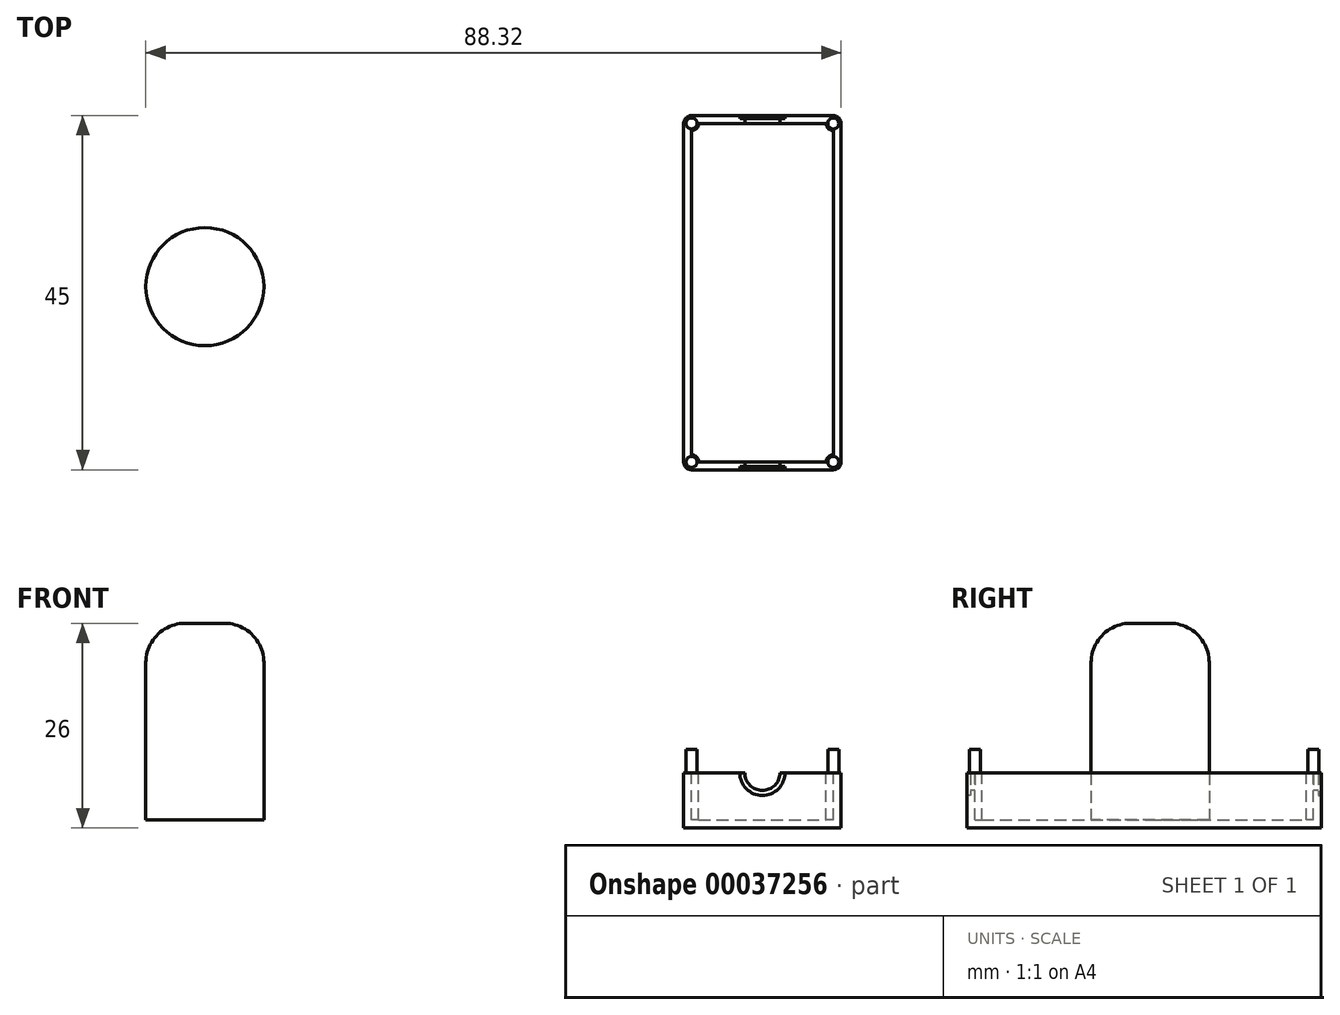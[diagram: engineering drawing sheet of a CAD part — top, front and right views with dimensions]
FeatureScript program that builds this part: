
annotation { "Feature Type Name" : "Feature", "Feature Type Description" : "" }
export const myFeature = defineFeature(function(context is Context, id is Id, definition is map)
    precondition{}
    {
        {
            var Q0;
            Q0=qCreatedBy(makeId("Top.planeOp"),FACE);
            var sketch = newSketch(context, id + "F0", { "sketchPlane" : qUnion([Q0])});
            skLineSegment(sketch, "E0.bottom", {"start": v(0, 0) * mm, "end": v(20, 0) * mm});
            skLineSegment(sketch, "E0.top", {"start": v(0, 45) * mm, "end": v(20, 45) * mm});
            skLineSegment(sketch, "E0.left", {"start": v(0, 0) * mm, "end": v(0, 45) * mm});
            skLineSegment(sketch, "E0.right", {"start": v(20, 0) * mm, "end": v(20, 45) * mm});
            skLineSegment(sketch, "E1.0", {"start": v(19, 1) * mm, "end": v(19, 44) * mm});
            skLineSegment(sketch, "E1.1", {"start": v(1, 1) * mm, "end": v(19, 1) * mm});
            skLineSegment(sketch, "E1.2", {"start": v(1, 1) * mm, "end": v(1, 44) * mm});
            skLineSegment(sketch, "E1.3", {"start": v(1, 44) * mm, "end": v(19, 44) * mm});
            skSolve(sketch);
        }
        {
            var Q0;
            Q0=makeQuery(id+"F0.imprint","IMPRINT",FACE,{"disambiguationData":[TD([[makeQuery(id+"F0.imprint","IMPRINT",EDGE,{"derivedFrom":sQuery(id+"F0.wireOp",EDGE,"E0.bottom")}),1.0]])]});
            extrude(context, id + "F1", {"entities" : qUnion([Q0]), "depth" : 6 * mm});
        }
        {
            var Q0;
            Q0=qCreatedBy(makeId("Top.planeOp"),FACE);
            var sketch = newSketch(context, id + "F2", { "sketchPlane" : qUnion([Q0])});
            skLineSegment(sketch, "E2.bottom", {"start": v(0, 0) * mm, "end": v(20, 0) * mm});
            skLineSegment(sketch, "E2.top", {"start": v(0, 45) * mm, "end": v(20, 45) * mm});
            skLineSegment(sketch, "E2.left", {"start": v(0, 0) * mm, "end": v(0, 45) * mm});
            skLineSegment(sketch, "E2.right", {"start": v(20, 0) * mm, "end": v(20, 45) * mm});
            skSolve(sketch);
        }
        {
            var Q0;
            Q0=makeQuery(id+"F2.imprint","IMPRINT",FACE,{"disambiguationData":[TD([[makeQuery(id+"F2.imprint","IMPRINT",EDGE,{"derivedFrom":sQuery(id+"F2.wireOp",EDGE,"E2.bottom")}),1.0]])]});
            extrude(context, id + "F3", {"entities" : qUnion([Q0]), "operationType" : NewBodyOperationType.ADD, "oppositeDirection" : true, "depth" : 1 * mm});
        }
        {
            var Q0;
            Q0=makeQuery(id+"F1.opExtrude","CAP_FACE",FACE,{"disambiguationData":[OSD([sQuery(id+"F0.wireOp",EDGE,"E0.bottom"),sQuery(id+"F0.wireOp",EDGE,"E0.top"),sQuery(id+"F0.wireOp",EDGE,"E0.left"),sQuery(id+"F0.wireOp",EDGE,"E0.right"),sQuery(id+"F0.wireOp",EDGE,"E1.0"),sQuery(id+"F0.wireOp",EDGE,"E1.1"),sQuery(id+"F0.wireOp",EDGE,"E1.2"),sQuery(id+"F0.wireOp",EDGE,"E1.3")])],"isStart":false});
            var sketch = newSketch(context, id + "F4", { "sketchPlane" : qUnion([Q0])});
            skCircle(sketch, "E3", {"center": v(19, 1) * mm, "radius": 0.9 * mm});
            skCircle(sketch, "E4", {"center": v(1, 44) * mm, "radius": 0.9 * mm});
            skCircle(sketch, "E5", {"center": v(19, 44) * mm, "radius": 0.9 * mm});
            skCircle(sketch, "E6", {"center": v(1, 1) * mm, "radius": 0.9 * mm});
            skSolve(sketch);
        }
        {
            var Q0;
            {var subQ1=sQuery(id+"F4.wireOp",EDGE,"E5");var subQ3=makeQuery(id+"F1.opExtrude","CAP_EDGE",EDGE,{"disambiguationData":[OSD([sQuery(id+"F0.wireOp",EDGE,"E1.0")])],"isStart":false});var subQ5=makeQuery(id+"F4.imprint","INTERSECT",VERTEX,{"derivedFrom":[subQ3,subQ1]});Q0=makeQuery(id+"F4.imprint","IMPRINT",FACE,{"disambiguationData":[TD([[makeQuery(id+"F4.imprint","IMPRINT",EDGE,{"disambiguationData":[TD([[subQ5,-1.0]])],"derivedFrom":subQ1}),1.0]])]});}
            var Q1;
            {var subQ1=sQuery(id+"F4.wireOp",EDGE,"E3");var subQ3=makeQuery(id+"F1.opExtrude","CAP_EDGE",EDGE,{"disambiguationData":[OSD([sQuery(id+"F0.wireOp",EDGE,"E1.0")])],"isStart":false});var subQ5=makeQuery(id+"F4.imprint","INTERSECT",VERTEX,{"derivedFrom":[subQ3,subQ1]});Q1=makeQuery(id+"F4.imprint","IMPRINT",FACE,{"disambiguationData":[TD([[makeQuery(id+"F4.imprint","IMPRINT",EDGE,{"disambiguationData":[TD([[subQ5,-1.0]])],"derivedFrom":subQ1}),1.0]])]});}
            var Q2;
            {var subQ1=sQuery(id+"F4.wireOp",EDGE,"E3");var subQ3=makeQuery(id+"F1.opExtrude","CAP_EDGE",EDGE,{"disambiguationData":[OSD([sQuery(id+"F0.wireOp",EDGE,"E1.0")])],"isStart":false});var subQ5=makeQuery(id+"F4.imprint","INTERSECT",VERTEX,{"derivedFrom":[subQ3,subQ1]});Q2=makeQuery(id+"F4.imprint","IMPRINT",FACE,{"disambiguationData":[TD([[makeQuery(id+"F4.imprint","IMPRINT",EDGE,{"disambiguationData":[TD([[subQ5,1.0]])],"derivedFrom":subQ1}),1.0]])]});}
            var Q3;
            {var subQ1=sQuery(id+"F4.wireOp",EDGE,"E6");var subQ3=makeQuery(id+"F1.opExtrude","CAP_EDGE",EDGE,{"disambiguationData":[OSD([sQuery(id+"F0.wireOp",EDGE,"E1.1")])],"isStart":false});var subQ5=makeQuery(id+"F4.imprint","INTERSECT",VERTEX,{"derivedFrom":[subQ3,subQ1]});Q3=makeQuery(id+"F4.imprint","IMPRINT",FACE,{"disambiguationData":[TD([[makeQuery(id+"F4.imprint","IMPRINT",EDGE,{"disambiguationData":[TD([[subQ5,-1.0]])],"derivedFrom":subQ1}),1.0]])]});}
            var Q4;
            {var subQ1=sQuery(id+"F4.wireOp",EDGE,"E4");var subQ3=makeQuery(id+"F1.opExtrude","CAP_EDGE",EDGE,{"disambiguationData":[OSD([sQuery(id+"F0.wireOp",EDGE,"E1.2")])],"isStart":false});var subQ5=makeQuery(id+"F4.imprint","INTERSECT",VERTEX,{"derivedFrom":[subQ3,subQ1]});Q4=makeQuery(id+"F4.imprint","IMPRINT",FACE,{"disambiguationData":[TD([[makeQuery(id+"F4.imprint","IMPRINT",EDGE,{"disambiguationData":[TD([[subQ5,-1.0]])],"derivedFrom":subQ1}),1.0]])]});}
            var Q5;
            {var subQ1=sQuery(id+"F4.wireOp",EDGE,"E5");var subQ3=makeQuery(id+"F1.opExtrude","CAP_EDGE",EDGE,{"disambiguationData":[OSD([sQuery(id+"F0.wireOp",EDGE,"E1.0")])],"isStart":false});var subQ5=makeQuery(id+"F4.imprint","INTERSECT",VERTEX,{"derivedFrom":[subQ3,subQ1]});Q5=makeQuery(id+"F4.imprint","IMPRINT",FACE,{"disambiguationData":[TD([[makeQuery(id+"F4.imprint","IMPRINT",EDGE,{"disambiguationData":[TD([[subQ5,1.0]])],"derivedFrom":subQ1}),1.0]])]});}
            extrude(context, id + "F5", {"entities" : qUnion([Q0, Q1, Q2, Q3, Q4, Q5]), "operationType" : NewBodyOperationType.ADD, "oppositeDirection" : true, "depth" : 6 * mm});
        }
        {
            var Q0;
            {var subQ0=sQuery(id+"F0.wireOp",EDGE,"E1.1");var subQ1=sQuery(id+"F0.wireOp",EDGE,"E1.2");var subQ2=sQuery(id+"F0.wireOp",EDGE,"E1.3");Q0=makeQuery(id+"F5.boolean.opBoolean","MERGE",FACE,{"derivedFrom":[makeQuery(id+"F1.opExtrude","CAP_FACE",FACE,{"disambiguationData":[OSD([sQuery(id+"F0.wireOp",EDGE,"E0.bottom"),sQuery(id+"F0.wireOp",EDGE,"E0.top"),sQuery(id+"F0.wireOp",EDGE,"E0.left"),sQuery(id+"F0.wireOp",EDGE,"E0.right"),sQuery(id+"F0.wireOp",EDGE,"E1.0"),subQ0,subQ1,subQ2])],"isStart":false}),makeQuery(id+"F5.opExtrude","CAP_FACE",FACE,{"disambiguationData":[OSD([sQuery(id+"F4.wireOp",EDGE,"E3")])],"isStart":true}),makeQuery(id+"F5.opExtrude","CAP_FACE",FACE,{"disambiguationData":[OSD([subQ1,subQ2,sQuery(id+"F4.wireOp",EDGE,"E4")])],"isStart":true}),makeQuery(id+"F5.opExtrude","CAP_FACE",FACE,{"disambiguationData":[OSD([sQuery(id+"F4.wireOp",EDGE,"E5")])],"isStart":true}),makeQuery(id+"F5.opExtrude","CAP_FACE",FACE,{"disambiguationData":[OSD([subQ0,subQ1,sQuery(id+"F4.wireOp",EDGE,"E6")])],"isStart":true})]});}
            var sketch = newSketch(context, id + "F6", { "sketchPlane" : qUnion([Q0])});
            skCircle(sketch, "E7", {"center": v(1, 1) * mm, "radius": 0.7 * mm});
            skCircle(sketch, "E8", {"center": v(19, 1) * mm, "radius": 0.7 * mm});
            skCircle(sketch, "E9", {"center": v(1, 44) * mm, "radius": 0.7 * mm});
            skCircle(sketch, "E10", {"center": v(19, 44) * mm, "radius": 0.7 * mm});
            skSolve(sketch);
        }
        {
            var Q0;
            Q0 = qSketchRegion(id + "F6", true);
            extrude(context, id + "F7", {"entities" : qUnion([Q0]), "operationType" : NewBodyOperationType.ADD, "depth" : 3 * mm});
        }
        {
            var Q0;
            Q0=makeQuery(id+"F3.boolean.opBoolean","MERGE",EDGE,{"derivedFrom":[makeQuery(id+"F1.opExtrude","SWEPT_EDGE",EDGE,{"disambiguationData":[OSD([sQuery(id+"F0.wireOp",EDGE,"E0.bottom"),sQuery(id+"F0.wireOp",EDGE,"E0.right")])]}),makeQuery(id+"F3.opExtrude","SWEPT_EDGE",EDGE,{"disambiguationData":[OSD([sQuery(id+"F2.wireOp",EDGE,"E2.bottom"),sQuery(id+"F2.wireOp",EDGE,"E2.right")])]})]});
            fillet(context, id + "F8", {"entities" : qUnion([Q0]), "radius" : 1 * mm, "allowEdgeOverflow" : false});
        }
        {
            var Q0;
            Q0=makeQuery(id+"F3.boolean.opBoolean","MERGE",EDGE,{"derivedFrom":[makeQuery(id+"F1.opExtrude","SWEPT_EDGE",EDGE,{"disambiguationData":[OSD([sQuery(id+"F0.wireOp",EDGE,"E0.bottom"),sQuery(id+"F0.wireOp",EDGE,"E0.left")])]}),makeQuery(id+"F3.opExtrude","SWEPT_EDGE",EDGE,{"disambiguationData":[OSD([sQuery(id+"F2.wireOp",EDGE,"E2.bottom"),sQuery(id+"F2.wireOp",EDGE,"E2.left")])]})]});
            fillet(context, id + "F9", {"entities" : qUnion([Q0]), "radius" : 1 * mm, "tangentPropagation" : true, "allowEdgeOverflow" : false});
        }
        {
            var Q0;
            Q0=makeQuery(id+"F3.boolean.opBoolean","MERGE",EDGE,{"derivedFrom":[makeQuery(id+"F1.opExtrude","SWEPT_EDGE",EDGE,{"disambiguationData":[OSD([sQuery(id+"F0.wireOp",EDGE,"E0.top"),sQuery(id+"F0.wireOp",EDGE,"E0.left")])]}),makeQuery(id+"F3.opExtrude","SWEPT_EDGE",EDGE,{"disambiguationData":[OSD([sQuery(id+"F2.wireOp",EDGE,"E2.top"),sQuery(id+"F2.wireOp",EDGE,"E2.left")])]})]});
            var Q1;
            Q1=makeQuery(id+"F3.boolean.opBoolean","MERGE",EDGE,{"derivedFrom":[makeQuery(id+"F1.opExtrude","SWEPT_EDGE",EDGE,{"disambiguationData":[OSD([sQuery(id+"F0.wireOp",EDGE,"E0.top"),sQuery(id+"F0.wireOp",EDGE,"E0.right")])]}),makeQuery(id+"F3.opExtrude","SWEPT_EDGE",EDGE,{"disambiguationData":[OSD([sQuery(id+"F2.wireOp",EDGE,"E2.top"),sQuery(id+"F2.wireOp",EDGE,"E2.right")])]})]});
            fillet(context, id + "F10", {"entities" : qUnion([Q0, Q1]), "radius" : 1 * mm, "tangentPropagation" : true, "allowEdgeOverflow" : false});
        }
        {
            var Q0;
            Q0=makeQuery(id+"F3.boolean.opBoolean","MERGE",FACE,{"derivedFrom":[makeQuery(id+"F1.opExtrude","SWEPT_FACE",FACE,{"disambiguationData":[OSD([sQuery(id+"F0.wireOp",EDGE,"E0.bottom")])]}),makeQuery(id+"F3.opExtrude","SWEPT_FACE",FACE,{"disambiguationData":[OSD([sQuery(id+"F2.wireOp",EDGE,"E2.bottom")])]})]});
            var sketch = newSketch(context, id + "F11", { "sketchPlane" : qUnion([Q0])});
            skCircle(sketch, "E11", {"center": v(10, 6) * mm, "radius": 2.87 * mm});
            skCircle(sketch, "E12", {"center": v(10, 6) * mm, "radius": 2.23 * mm});
            skSolve(sketch);
        }
        {
            var Q0;
            Q0=makeQuery(id+"F3.boolean.opBoolean","MERGE",FACE,{"derivedFrom":[makeQuery(id+"F1.opExtrude","SWEPT_FACE",FACE,{"disambiguationData":[OSD([sQuery(id+"F0.wireOp",EDGE,"E0.top")])]}),makeQuery(id+"F3.opExtrude","SWEPT_FACE",FACE,{"disambiguationData":[OSD([sQuery(id+"F2.wireOp",EDGE,"E2.top")])]})]});
            var sketch = newSketch(context, id + "F12", { "sketchPlane" : qUnion([Q0])});
            skCircle(sketch, "E13", {"center": v(-10, 6) * mm, "radius": 2.23 * mm});
            skCircle(sketch, "E14", {"center": v(-10, 6) * mm, "radius": 2.87 * mm});
            skSolve(sketch);
        }
        {
            var Q0;
            {var subQ0=makeQuery(id+"F1.opExtrude","CAP_EDGE",EDGE,{"disambiguationData":[OSD([sQuery(id+"F0.wireOp",EDGE,"E0.bottom")])],"isStart":false});var subQ1=sQuery(id+"F11.wireOp",EDGE,"E12");var subQ3=makeQuery(id+"F11.imprint","INTERSECT",VERTEX,{"disambiguationData":[OD(0.0)],"derivedFrom":[subQ0,subQ1]});Q0=makeQuery(id+"F11.imprint","IMPRINT",FACE,{"disambiguationData":[TD([[makeQuery(id+"F11.imprint","IMPRINT",EDGE,{"disambiguationData":[TD([[subQ3,1.0]])],"derivedFrom":subQ1}),1.0]])]});}
            extrude(context, id + "F13", {"entities" : qUnion([Q0]), "operationType" : NewBodyOperationType.REMOVE, "endBound" : BoundingType.THROUGH_ALL, "oppositeDirection" : true, "depth" : 25 * mm});
        }
        {
            var Q0;
            {var subQ0=makeQuery(id+"F1.opExtrude","CAP_EDGE",EDGE,{"disambiguationData":[OSD([sQuery(id+"F0.wireOp",EDGE,"E0.bottom")])],"isStart":false});var subQ3=sQuery(id+"F11.wireOp",EDGE,"E11");var subQ6=makeQuery(id+"F11.imprint","INTERSECT",VERTEX,{"disambiguationData":[OD(0.0)],"derivedFrom":[subQ0,subQ3]});Q0=makeQuery(id+"F11.imprint","IMPRINT",FACE,{"disambiguationData":[TD([[makeQuery(id+"F11.imprint","IMPRINT",EDGE,{"disambiguationData":[TD([[subQ6,1.0]])],"derivedFrom":subQ3}),1.0]])]});}
            extrude(context, id + "F14", {"entities" : qUnion([Q0]), "operationType" : NewBodyOperationType.REMOVE, "oppositeDirection" : true, "depth" : 0.4 * mm});
        }
        {
            var Q0;
            {var subQ0=makeQuery(id+"F1.opExtrude","CAP_EDGE",EDGE,{"disambiguationData":[OSD([sQuery(id+"F0.wireOp",EDGE,"E0.top")])],"isStart":false});var subQ1=sQuery(id+"F12.wireOp",EDGE,"E13");var subQ5=makeQuery(id+"F12.imprint","INTERSECT",VERTEX,{"disambiguationData":[OD(0.0)],"derivedFrom":[subQ0,subQ1]});Q0=makeQuery(id+"F12.imprint","IMPRINT",FACE,{"disambiguationData":[TD([[makeQuery(id+"F12.imprint","IMPRINT",EDGE,{"disambiguationData":[TD([[subQ5,1.0]])],"derivedFrom":subQ1}),-1.0]])]});}
            extrude(context, id + "F15", {"entities" : qUnion([Q0]), "operationType" : NewBodyOperationType.REMOVE, "oppositeDirection" : true, "depth" : .4 * mm});
        }
        {
            var Q0;
            Q0=qCreatedBy(makeId("Top.planeOp"),FACE);
            var sketch = newSketch(context, id + "F16", { "sketchPlane" : qUnion([Q0])});
            skCircle(sketch, "E15", {"center": v(-60.82, 23.26) * mm, "radius": 7.5 * mm});
            skSolve(sketch);
        }
        {
            var Q0;
            Q0=makeQuery(id+"F16.imprint","IMPRINT",FACE,{"disambiguationData":[TD([[makeQuery(id+"F16.imprint","IMPRINT",EDGE,{"derivedFrom":sQuery(id+"F16.wireOp",EDGE,"E15")}),1.0]])]});
            extrude(context, id + "F17", {"entities" : qUnion([Q0]), "depth" : 25 * mm});
        }
        {
            var Q0;
            Q0=makeQuery(id+"F17.opExtrude","CAP_EDGE",EDGE,{"disambiguationData":[OSD([sQuery(id+"F16.wireOp",EDGE,"E15")])],"isStart":false});
            fillet(context, id + "F18", {"entities" : qUnion([Q0]), "radius" : 5 * mm, "tangentPropagation" : true, "allowEdgeOverflow" : false});
        }
    });
